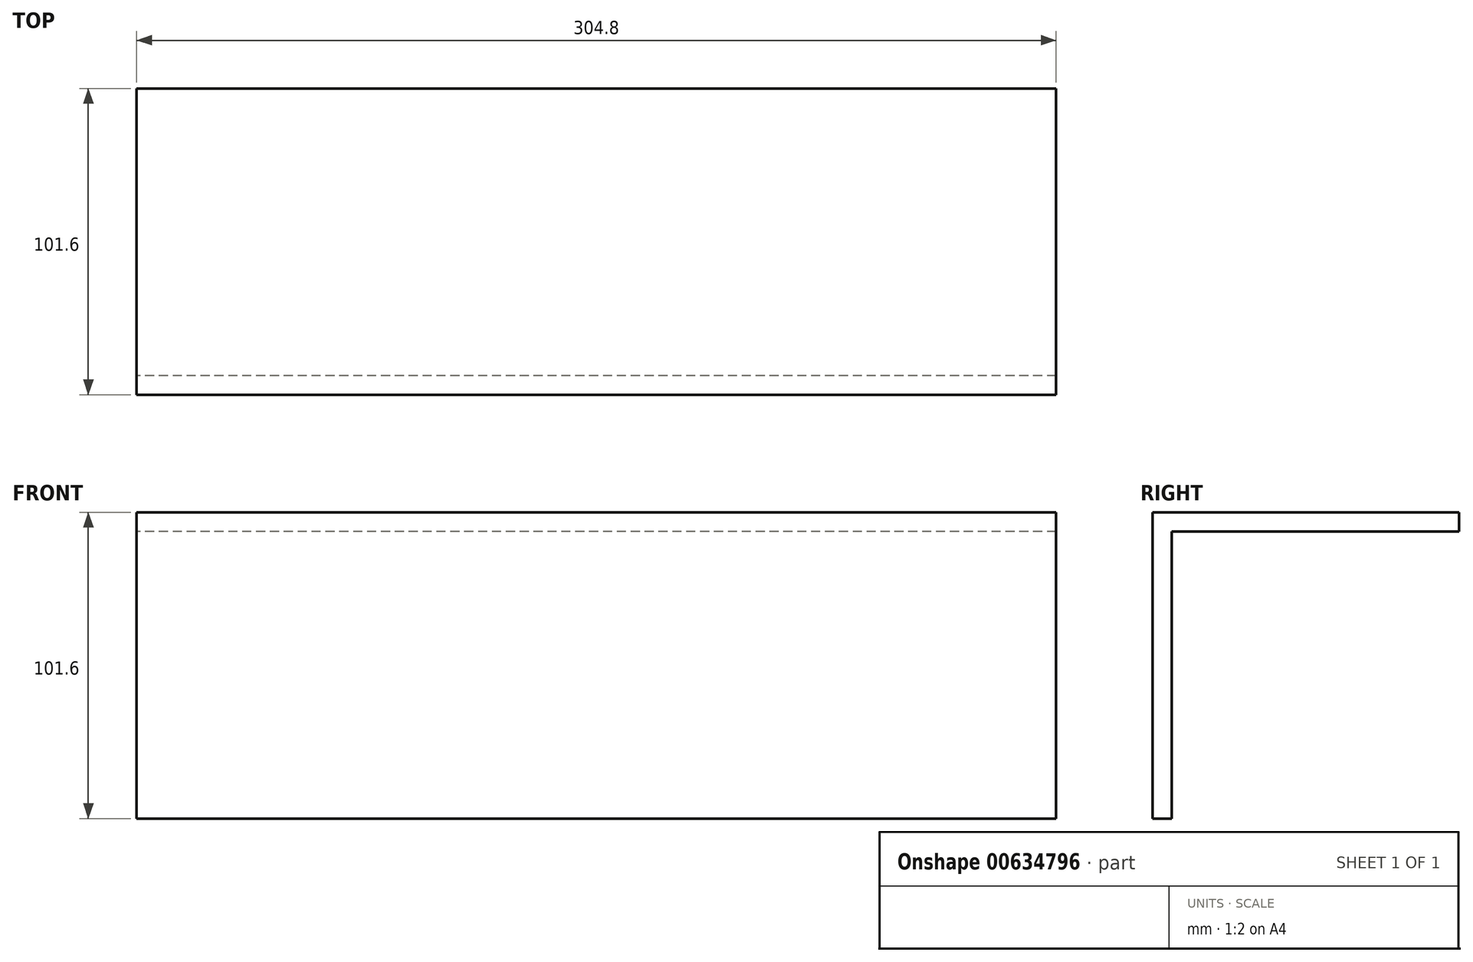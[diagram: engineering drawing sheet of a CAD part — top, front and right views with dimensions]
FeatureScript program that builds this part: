
annotation { "Feature Type Name" : "Feature", "Feature Type Description" : "" }
export const myFeature = defineFeature(function(context is Context, id is Id, definition is map)
    precondition{}
    {
        {
            var Q0;
            Q0=qCreatedBy(makeId("Right.planeOp"),FACE);
            var sketch = newSketch(context, id + "F0", { "sketchPlane" : qUnion([Q0])});
            skLineSegment(sketch, "E0", {"start": v(0, 0) * mm, "end": v(101.6, 0) * mm});
            skLineSegment(sketch, "E1", {"start": v(101.6, 0) * mm, "end": v(101.6, -6.35) * mm});
            skLineSegment(sketch, "E2", {"start": v(101.6, -6.35) * mm, "end": v(6.35, -6.35) * mm});
            skLineSegment(sketch, "E3", {"start": v(6.35, -6.35) * mm, "end": v(6.35, -101.6) * mm});
            skLineSegment(sketch, "E4", {"start": v(6.35, -101.6) * mm, "end": v(0, -101.6) * mm});
            skLineSegment(sketch, "E5", {"start": v(0, -101.6) * mm, "end": v(0, 0) * mm});
            skSolve(sketch);
        }
        {
            var Q0;
            Q0=makeQuery(id+"F0.imprint","IMPRINT",FACE,{"disambiguationData":[TD([[makeQuery(id+"F0.imprint","IMPRINT",EDGE,{"derivedFrom":sQuery(id+"F0.wireOp",EDGE,"E0")}),-1.0]])]});
            extrude(context, id + "F1", {"entities" : qUnion([Q0]), "endBound" : BoundingType.SYMMETRIC, "depth" : 304.8 * mm, "offsetDistance" : 25.4 * mm});
        }
    });
